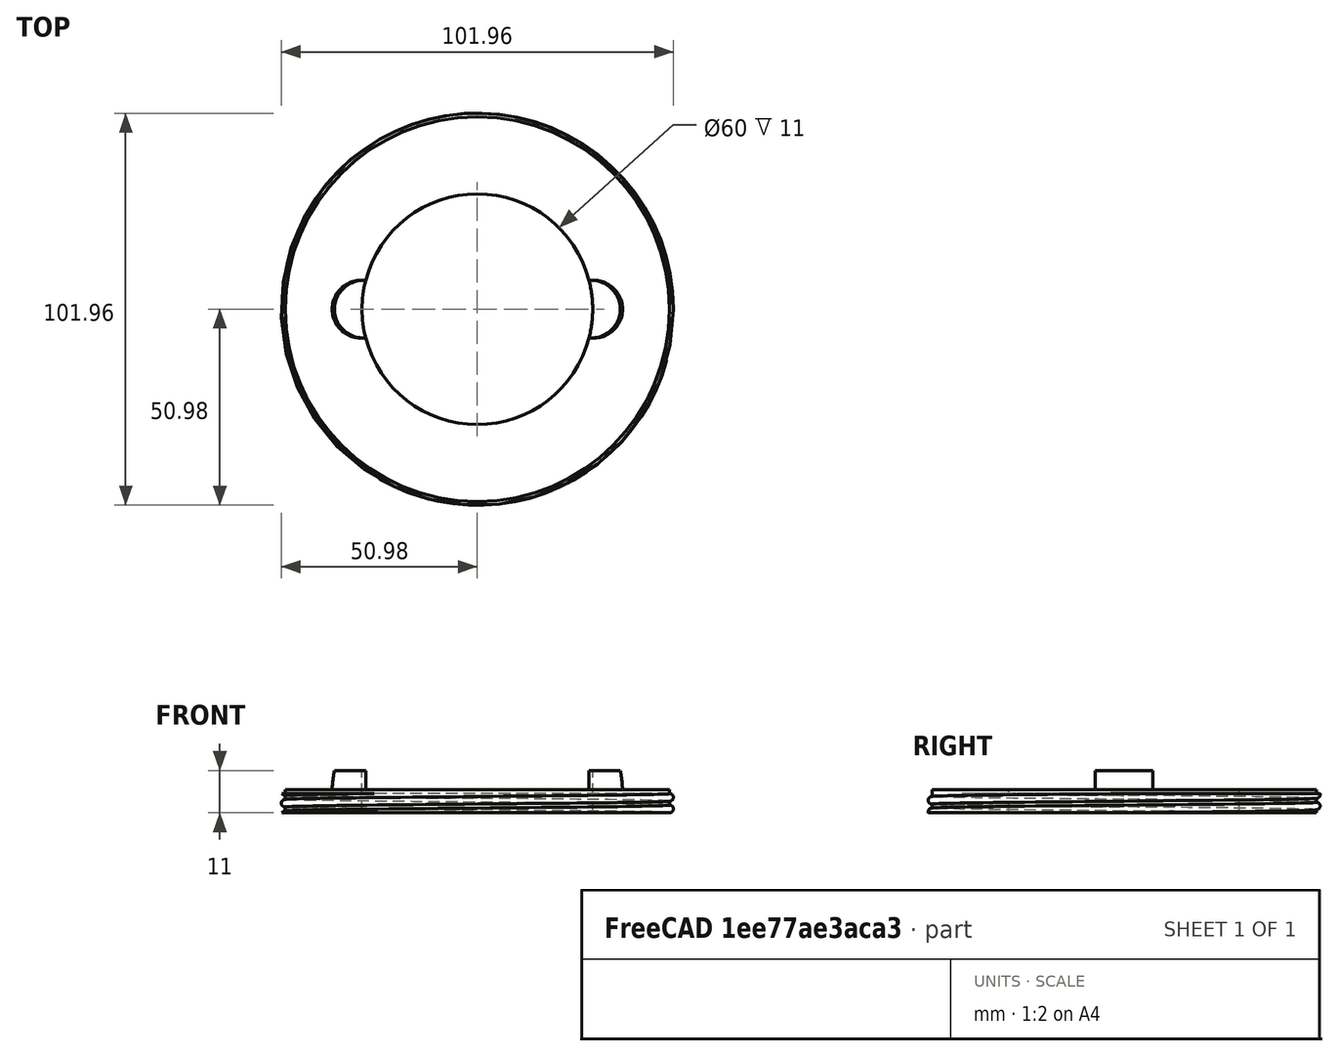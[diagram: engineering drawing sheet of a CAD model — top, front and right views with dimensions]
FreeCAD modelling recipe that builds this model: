
FCSTD DOCUMENT  (FreeCAD 0.17R13522 (Git))
Label: test_tapa
License: CreativeCommons Attribution-ShareAlike
LicenseURL: http://creativecommons.org/licenses/by-sa/4.0/
objects: Part::Cut×2, Part::Feature×1, Part::Box×1, Part::Cylinder×1
note: 5 computed .brp shape members not serialized (recipe doc carries the construction recipe); baked Part::Feature solids carry a one-line shape summary decoded from their .brp

FEATURE [Part::Feature] Fusion008001  label="tapa_con_rosca_099"
  shape: bbox 108.9 x 117.3 x 45.68 mm, 15 faces (baked)
FEATURE [Part::Box] Box  label="Cube"
  AttacherType = Attacher::AttachEngine3D
  Height = 50
  Length = 500
  Placement = pos=(-108,-81,114) rot=(0,0,1;0rad)
  Width = 500
FEATURE [Part::Cut] Cut
  Base = -> Fusion008001
  Tool = -> Box
FEATURE [Part::Cylinder] Cylinder
  Angle = 360
  AttacherType = Attacher::AttachEngine3D
  Height = 20
  Placement = pos=(0,0,97) rot=(0,0,1;0rad)
  Radius = 30
FEATURE [Part::Cut] Cut001
  Base = -> Cut
  Tool = -> Cylinder
